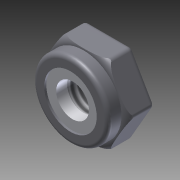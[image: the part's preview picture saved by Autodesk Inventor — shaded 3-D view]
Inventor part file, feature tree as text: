
AUTODESK INVENTOR PART (.ipt)
format: ipt  version: 2011 (Build 150239000, 239)  size: 185,856 bytes
history: native  units: in
note: dims shown in document units (in); Inventor stores cm internally (conversion verified against a paired STEP export)
features: sketch x5, extrude x3, fillet x2, hole x1, revolve x1, projected_geometry x1
ambient origin geometry x8: Origin, YZ Plane, XZ Plane, XY Plane, X Axis, Y Axis, Z Axis, Center Point
bodies: Solid1 (feature_tree)
feature tree (13):
  extrude  "Extrusion1"  Depth=0.125in TaperAngle=0.0deg
  extrude  "Extrusion2"  Depth=0.0625in TaperAngle=0.0deg
  extrude  "Extrusion3"  Depth=0.01in TaperAngle=0.0deg
  hole  "Hole2"  [1 undecoded]
  revolve  "Revolution2"  [1 undecoded]
  fillet  "Fillet1"  Radius=0.02in
  fillet  "Fillet2"  [1 undecoded]
  sketch  "Sketch1"  dims[d0=0.375in d1=0.125in d2=0.0in]
  sketch  "Sketch3"  dims[d3=0.36in d4=0.0625in d5=0.0in]
  sketch  "Sketch8"  dims[d14=0.25in d15=0.01in d16=0.0in]
  sketch  "Sketch9"  dims[d17=0.156in d18=0.125in d19=0.375in d20=0.25in d21=0.5635in d22=1.0in d23=0.8108in d24=0.18in]
  sketch  "Sketch10"  dims[d25=90.0deg d26=0.02in d27=0.02in]
  projected_geometry  "Projected Loop8"
note: 3 required parameter values undecoded (feature->parameter linkage not recoverable at this tier; creation-order binding heuristic only, values carry confidence <= 0.55)